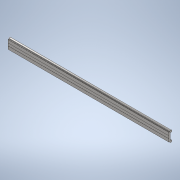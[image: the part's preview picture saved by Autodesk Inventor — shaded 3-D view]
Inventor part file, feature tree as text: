
AUTODESK INVENTOR PART (.ipt)
format: ipt  version: 2020 (Build 240168000, 168)  size: 124,416 bytes
history: native  units: mm
features: other x1, extrude x1, sketch x1
ambient origin geometry x8: Origin, YZ Plane, XZ Plane, XY Plane, X Axis, Y Axis, Z Axis, Center Point
bodies: Body1 (feature_tree)
feature tree (3):
  other  "Bryła1"
  extrude  "Wyciągnięcie proste1"  Depth=750.0mm TaperAngle=0.0deg
  sketch  "Szkic1"
